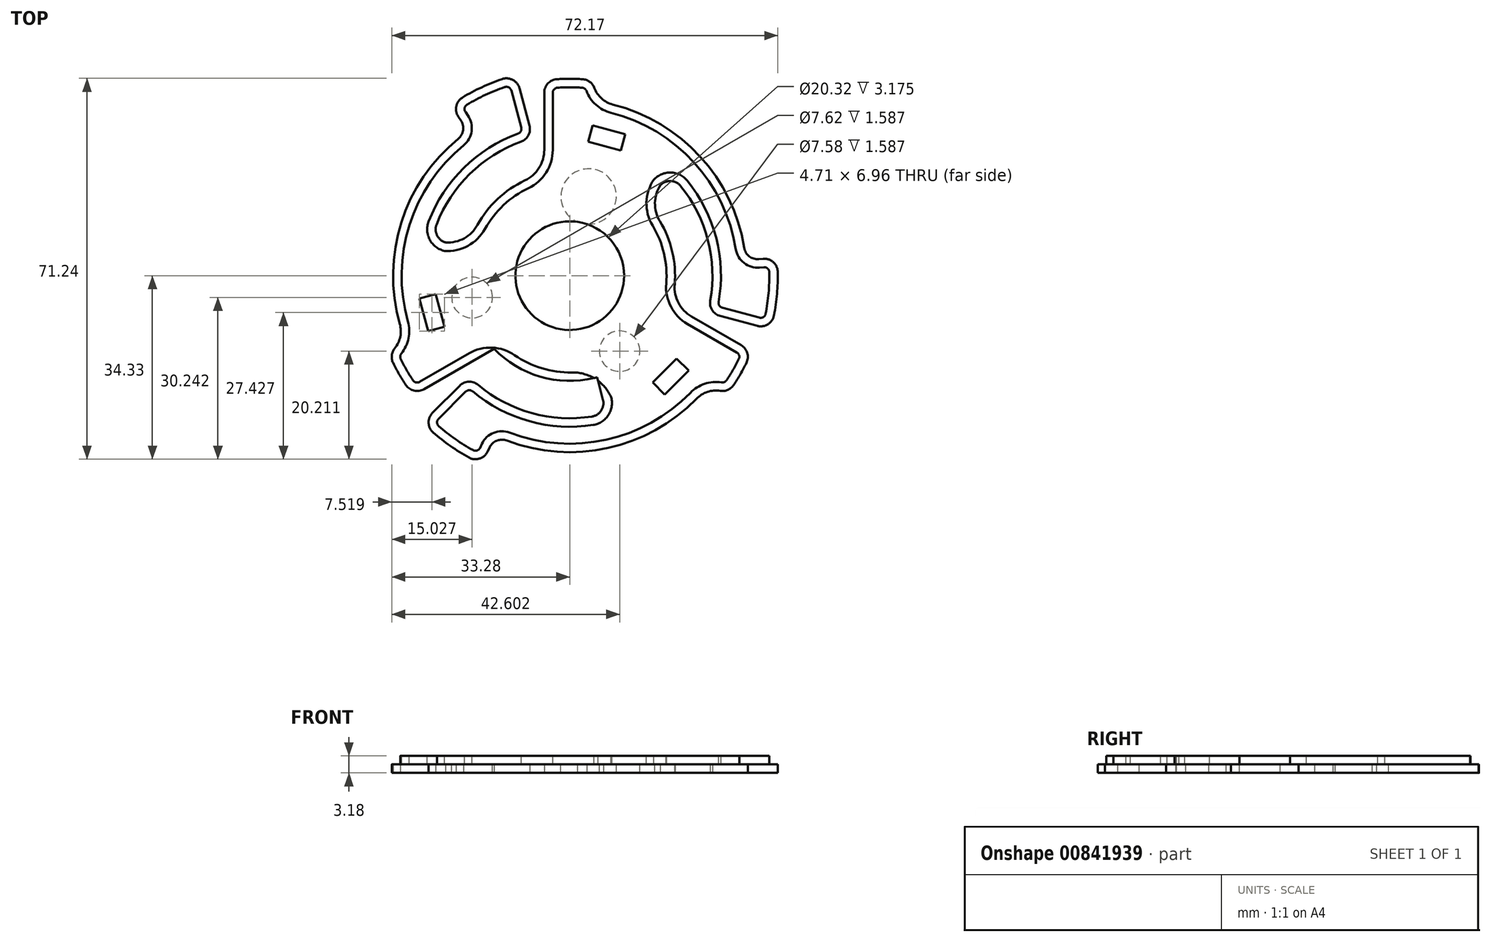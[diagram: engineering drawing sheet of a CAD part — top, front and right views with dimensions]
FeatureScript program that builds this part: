
annotation { "Feature Type Name" : "Feature", "Feature Type Description" : "" }
export const myFeature = defineFeature(function(context is Context, id is Id, definition is map)
    precondition{}
    {
        {
            var Q0;
            Q0=qCreatedBy(makeId("Top.planeOp"),FACE);
            var sketch = newSketch(context, id + "F0", { "sketchPlane" : qUnion([Q0])});
            skCircle(sketch, "E0", {"center": v(0, 0) * mm, "radius": 38.9 * mm, "construction": true});
            skCircle(sketch, "E1", {"center": v(0, 0) * mm, "radius": 36.83 * mm, "construction": true});
            skCircle(sketch, "E2", {"center": v(0, 0) * mm, "radius": 10.16 * mm});
            skCircle(sketch, "E3", {"center": v(0, 0) * mm, "radius": 19.69 * mm});
            skCircle(sketch, "E4", {"center": v(0, 0) * mm, "radius": 33.02 * mm, "construction": true});
            skLineSegment(sketch, "E5", {"start": v(-4.76, 19.1) * mm, "end": v(-4.76, 36.52) * mm});
            skLineSegment(sketch, "E6", {"start": v(0, 0) * mm, "end": v(0, 38.9) * mm, "construction": true});
            skLineSegment(sketch, "E7", {"start": v(4.76, 36.52) * mm, "end": v(4.76, 32.67) * mm});
            skArc(sketch, "E8", {"start": v(4.76, 36.52) * mm, "mid": v(0, 36.83) * mm, "end": v(-4.76, 36.52) * mm});
            skLineSegment(sketch, "E9", {"start": v(32.9, 2.88) * mm, "end": v(38.75, 3.39) * mm});
            skLineSegment(sketch, "E10", {"start": v(37.57, -10.07) * mm, "end": v(25.76, -6.9) * mm});
            skCircle(sketch, "E11.0", {"center": v(0, 0) * mm, "radius": 26.67 * mm, "construction": true});
            skArc(sketch, "E12", {"start": v(37.57, -10.07) * mm, "mid": v(38.75, -3.39) * mm, "end": v(38.75, 3.39) * mm});
            skArc(sketch, "E13", {"start": v(32.9, 2.88) * mm, "mid": v(24, 22.67) * mm, "end": v(4.76, 32.67) * mm});
            skArc(sketch, "E14", {"start": v(25.76, -6.9) * mm, "mid": v(25.76, 6.9) * mm, "end": v(18.86, 18.86) * mm});
            skLineSegment(sketch, "E15", {"start": v(18.86, 18.86) * mm, "end": v(13.92, 13.92) * mm});
            skLineSegment(sketch, "E16.bottom", {"start": v(9.56, 23.4) * mm, "end": v(3.43, 25.05) * mm});
            skLineSegment(sketch, "E16.top", {"start": v(10.38, 26.47) * mm, "end": v(4.25, 28.12) * mm});
            skLineSegment(sketch, "E16.left", {"start": v(9.56, 23.4) * mm, "end": v(10.38, 26.47) * mm});
            skLineSegment(sketch, "E16.right", {"start": v(3.43, 25.05) * mm, "end": v(4.25, 28.12) * mm});
            skPoint(sketch, "E16.middle", {"position": v(6.9, 25.76) * mm});
            skLineSegment(sketch, "E17", {"start": v(7.31, 27.3) * mm, "end": v(0, 0) * mm, "construction": true});
            skSolve(sketch);
        }
        {
            var Q0;
            {var subQ0=sQuery(id+"F0.wireOp",EDGE,"E5");Q0=makeQuery(id+"F0.imprint","IMPRINT",FACE,{"disambiguationData":[TD([[makeQuery(id+"F0.imprint","IMPRINT",EDGE,{"derivedFrom":subQ0}),-1.0]])]});}
            extrude(context, id + "F1", {"entities" : qUnion([Q0]), "depth" : 3.17 * mm, "offsetDistance" : 25.4 * mm});
        }
        {
            var Q0;
            Q0=makeQuery(id+"F1.opExtrude","SWEPT_EDGE",EDGE,{"disambiguationData":[OSD([sQuery(id+"F0.wireOp",EDGE,"E5"),sQuery(id+"F0.wireOp",EDGE,"E8")])]});
            var Q1;
            Q1=makeQuery(id+"F1.opExtrude","SWEPT_EDGE",EDGE,{"disambiguationData":[OSD([sQuery(id+"F0.wireOp",EDGE,"E7"),sQuery(id+"F0.wireOp",EDGE,"E8")])]});
            var Q2;
            Q2=makeQuery(id+"F1.opExtrude","SWEPT_EDGE",EDGE,{"disambiguationData":[OSD([sQuery(id+"F0.wireOp",EDGE,"E9"),sQuery(id+"F0.wireOp",EDGE,"E13")])]});
            var Q3;
            Q3=makeQuery(id+"F1.opExtrude","SWEPT_EDGE",EDGE,{"disambiguationData":[OSD([sQuery(id+"F0.wireOp",EDGE,"E9"),sQuery(id+"F0.wireOp",EDGE,"E12")])]});
            var Q4;
            Q4=makeQuery(id+"F1.opExtrude","SWEPT_EDGE",EDGE,{"disambiguationData":[OSD([sQuery(id+"F0.wireOp",EDGE,"E10"),sQuery(id+"F0.wireOp",EDGE,"E12")])]});
            var Q5;
            Q5=makeQuery(id+"F1.opExtrude","SWEPT_EDGE",EDGE,{"disambiguationData":[OSD([sQuery(id+"F0.wireOp",EDGE,"E10"),sQuery(id+"F0.wireOp",EDGE,"E14")])]});
            var Q6;
            Q6=makeQuery(id+"F1.opExtrude","SWEPT_EDGE",EDGE,{"disambiguationData":[OSD([sQuery(id+"F0.wireOp",EDGE,"E14"),sQuery(id+"F0.wireOp",EDGE,"E15")])]});
            fillet(context, id + "F2", {"entities" : qUnion([Q0, Q1, Q2, Q3, Q4, Q5, Q6]), "radius" : 2.54 * mm, "tangentPropagation" : true, "allowEdgeOverflow" : false});
        }
        {
            var Q0;
            Q0=makeQuery(id+"F1.opExtrude","SWEPT_EDGE",EDGE,{"disambiguationData":[OSD([sQuery(id+"F0.wireOp",EDGE,"E7"),sQuery(id+"F0.wireOp",EDGE,"E13")])]});
            fillet(context, id + "F3", {"entities" : qUnion([Q0]), "radius" : 5.08 * mm, "tangentPropagation" : true, "allowEdgeOverflow" : false});
        }
        {
            var Q0;
            Q0=makeQuery(id+"F1.opExtrude","SWEPT_BODY",BODY,{"disambiguationData":[OSD([sQuery(id+"F0.wireOp",EDGE,"E3"),sQuery(id+"F0.wireOp",EDGE,"E5"),sQuery(id+"F0.wireOp",EDGE,"E7"),sQuery(id+"F0.wireOp",EDGE,"E8"),sQuery(id+"F0.wireOp",EDGE,"E9"),sQuery(id+"F0.wireOp",EDGE,"E10"),sQuery(id+"F0.wireOp",EDGE,"E12"),sQuery(id+"F0.wireOp",EDGE,"E13"),sQuery(id+"F0.wireOp",EDGE,"E14"),sQuery(id+"F0.wireOp",EDGE,"E15")])]});
            var Q1;
            Q1=makeQuery(id+"F1.opExtrude","SWEPT_FACE",FACE,{"disambiguationData":[OSD([sQuery(id+"F0.wireOp",EDGE,"E3")])]});
            circularPattern(context, id + "F4", {"entities" : qUnion([Q0]), "axis" : qUnion([Q1]), "angle" : 360 * degree, "instanceCount" : 3, "oppositeDirection" : true, "equalSpace" : true});
        }
        {
            var Q0;
            Q0=makeQuery(id+"F0.imprint","IMPRINT",FACE,{"disambiguationData":[TD([[makeQuery(id+"F0.imprint","IMPRINT",EDGE,{"derivedFrom":sQuery(id+"F0.wireOp",EDGE,"E2")}),-1.0]])]});
            extrude(context, id + "F5", {"entities" : qUnion([Q0]), "operationType" : NewBodyOperationType.ADD, "depth" : 3.17 * mm, "offsetDistance" : 25.4 * mm});
        }
        {
            var Q0;
            Q0=makeQuery(id+"F1.opExtrude","SWEPT_EDGE",EDGE,{"disambiguationData":[OSD([sQuery(id+"F0.wireOp",EDGE,"E3"),sQuery(id+"F0.wireOp",EDGE,"E15")])]});
            var Q1;
            Q1=makeQuery(id+"F4.opPattern","COPY",EDGE,{"derivedFrom":makeQuery(id+"F1.opExtrude","SWEPT_EDGE",EDGE,{"disambiguationData":[OSD([sQuery(id+"F0.wireOp",EDGE,"E3"),sQuery(id+"F0.wireOp",EDGE,"E5")])]}),"instanceName":"1"});
            var Q2;
            Q2=makeQuery(id+"F4.opPattern","COPY",EDGE,{"derivedFrom":makeQuery(id+"F1.opExtrude","SWEPT_EDGE",EDGE,{"disambiguationData":[OSD([sQuery(id+"F0.wireOp",EDGE,"E3"),sQuery(id+"F0.wireOp",EDGE,"E15")])]}),"instanceName":"1"});
            var Q3;
            Q3=makeQuery(id+"F4.opPattern","COPY",EDGE,{"derivedFrom":makeQuery(id+"F1.opExtrude","SWEPT_EDGE",EDGE,{"disambiguationData":[OSD([sQuery(id+"F0.wireOp",EDGE,"E3"),sQuery(id+"F0.wireOp",EDGE,"E5")])]}),"instanceName":"2"});
            var Q4;
            Q4=makeQuery(id+"F4.opPattern","COPY",EDGE,{"derivedFrom":makeQuery(id+"F1.opExtrude","SWEPT_EDGE",EDGE,{"disambiguationData":[OSD([sQuery(id+"F0.wireOp",EDGE,"E3"),sQuery(id+"F0.wireOp",EDGE,"E15")])]}),"instanceName":"2"});
            var Q5;
            Q5=makeQuery(id+"F1.opExtrude","SWEPT_EDGE",EDGE,{"disambiguationData":[OSD([sQuery(id+"F0.wireOp",EDGE,"E3"),sQuery(id+"F0.wireOp",EDGE,"E5")])]});
            fillet(context, id + "F6", {"entities" : qUnion([Q0, Q1, Q2, Q3, Q4, Q5]), "radius" : 6.35 * mm, "tangentPropagation" : true, "allowEdgeOverflow" : false});
        }
        {
            var Q0;
            {var subQ0=sQuery(id+"F0.wireOp",EDGE,"E3");var subQ1=makeQuery(id+"F1.opExtrude","CAP_FACE",FACE,{"disambiguationData":[OSD([subQ0,sQuery(id+"F0.wireOp",EDGE,"E5"),sQuery(id+"F0.wireOp",EDGE,"E7"),sQuery(id+"F0.wireOp",EDGE,"E8"),sQuery(id+"F0.wireOp",EDGE,"E9"),sQuery(id+"F0.wireOp",EDGE,"E10"),sQuery(id+"F0.wireOp",EDGE,"E12"),sQuery(id+"F0.wireOp",EDGE,"E13"),sQuery(id+"F0.wireOp",EDGE,"E14"),sQuery(id+"F0.wireOp",EDGE,"E15")])],"isStart":false});Q0=makeQuery(id+"F5.boolean.opBoolean","MERGE",FACE,{"derivedFrom":[subQ1,makeQuery(id+"F4.opPattern","COPY",FACE,{"derivedFrom":subQ1,"instanceName":"1"}),makeQuery(id+"F4.opPattern","COPY",FACE,{"derivedFrom":subQ1,"instanceName":"2"}),makeQuery(id+"F5.opExtrude","CAP_FACE",FACE,{"disambiguationData":[OSD([sQuery(id+"F0.wireOp",EDGE,"E2"),subQ0])],"isStart":false})]});}
            var sketch = newSketch(context, id + "F7", { "sketchPlane" : qUnion([Q0])});
            skArc(sketch, "E18.0.0", {"start": v(20.74, 16.77) * mm, "mid": v(25.82, 6.67) * mm, "end": v(26.26, -4.64) * mm});
            skArc(sketch, "E18.0.1", {"start": v(26.26, -4.64) * mm, "mid": v(26.62, -6.44) * mm, "end": v(28.1, -7.53) * mm});
            skLineSegment(sketch, "E18.0.2", {"start": v(28.1, -7.53) * mm, "end": v(35.03, -9.39) * mm});
            skArc(sketch, "E18.0.3", {"start": v(35.03, -9.39) * mm, "mid": v(37.03, -9.09) * mm, "end": v(38.18, -7.42) * mm});
            skArc(sketch, "E18.0.4", {"start": v(38.18, -7.42) * mm, "mid": v(38.75, -3.39) * mm, "end": v(38.89, 0.67) * mm});
            skArc(sketch, "E18.0.5", {"start": v(38.89, 0.67) * mm, "mid": v(38.05, 2.52) * mm, "end": v(36.13, 3.16) * mm});
            skLineSegment(sketch, "E18.0.6", {"start": v(36.13, 3.16) * mm, "end": v(35.33, 3.1) * mm});
            skArc(sketch, "E18.0.7", {"start": v(35.33, 3.1) * mm, "mid": v(33.55, 3.62) * mm, "end": v(32.6, 5.22) * mm});
            skArc(sketch, "E18.0.8", {"start": v(32.6, 5.22) * mm, "mid": v(24.36, 22.29) * mm, "end": v(8.1, 32.01) * mm});
            skArc(sketch, "E18.0.9", {"start": v(8.1, 32.01) * mm, "mid": v(5.97, 33.14) * mm, "end": v(4.6, 35.12) * mm});
            skArc(sketch, "E18.0.10", {"start": v(4.6, 35.12) * mm, "mid": v(3.73, 36.26) * mm, "end": v(2.39, 36.75) * mm});
            skArc(sketch, "E18.0.11", {"start": v(2.39, 36.75) * mm, "mid": v(0, 36.83) * mm, "end": v(-2.39, 36.75) * mm});
            skArc(sketch, "E18.0.12", {"start": v(-2.39, 36.75) * mm, "mid": v(-4.08, 35.95) * mm, "end": v(-4.76, 34.22) * mm});
            skLineSegment(sketch, "E18.0.13", {"start": v(-4.76, 34.22) * mm, "end": v(-4.76, 23.54) * mm});
            skArc(sketch, "E18.0.14", {"start": v(-4.76, 23.54) * mm, "mid": v(-5.75, 20.14) * mm, "end": v(-8.4, 17.8) * mm});
            skArc(sketch, "E18.0.15", {"start": v(-8.4, 17.8) * mm, "mid": v(-13.48, 14.34) * mm, "end": v(-17.25, 9.49) * mm});
            skArc(sketch, "E18.0.16", {"start": v(-17.25, 9.49) * mm, "mid": v(-19.74, 7) * mm, "end": v(-23.18, 6.21) * mm});
            skArc(sketch, "E18.0.17", {"start": v(-23.18, 6.21) * mm, "mid": v(-24.78, 7.51) * mm, "end": v(-24.9, 9.58) * mm});
            skArc(sketch, "E18.0.18", {"start": v(-24.9, 9.58) * mm, "mid": v(-18.68, 19.03) * mm, "end": v(-9.12, 25.06) * mm});
            skArc(sketch, "E18.0.19", {"start": v(-9.12, 25.06) * mm, "mid": v(-7.73, 26.28) * mm, "end": v(-7.53, 28.1) * mm});
            skLineSegment(sketch, "E18.0.20", {"start": v(-7.53, 28.1) * mm, "end": v(-9.39, 35.03) * mm});
            skArc(sketch, "E18.0.21", {"start": v(-9.39, 35.03) * mm, "mid": v(-10.65, 36.61) * mm, "end": v(-12.67, 36.77) * mm});
            skArc(sketch, "E18.0.22", {"start": v(-12.67, 36.77) * mm, "mid": v(-16.44, 35.25) * mm, "end": v(-20.03, 33.34) * mm});
            skArc(sketch, "E18.0.23", {"start": v(-20.03, 33.34) * mm, "mid": v(-21.2, 31.7) * mm, "end": v(-20.8, 29.7) * mm});
            skLineSegment(sketch, "E18.0.24", {"start": v(-20.8, 29.7) * mm, "end": v(-20.34, 29.05) * mm});
            skArc(sketch, "E18.0.25", {"start": v(-20.34, 29.05) * mm, "mid": v(-19.9, 27.25) * mm, "end": v(-20.82, 25.63) * mm});
            skArc(sketch, "E18.0.26", {"start": v(-20.82, 25.63) * mm, "mid": v(-31.48, 9.96) * mm, "end": v(-31.77, -9) * mm});
            skArc(sketch, "E18.0.27", {"start": v(-31.77, -9) * mm, "mid": v(-31.68, -11.4) * mm, "end": v(-32.72, -13.58) * mm});
            skArc(sketch, "E18.0.28", {"start": v(-32.72, -13.58) * mm, "mid": v(-33.27, -14.9) * mm, "end": v(-33.02, -16.3) * mm});
            skArc(sketch, "E18.0.29", {"start": v(-33.02, -16.3) * mm, "mid": v(-31.9, -18.42) * mm, "end": v(-30.64, -20.44) * mm});
            skArc(sketch, "E18.0.30", {"start": v(-30.64, -20.44) * mm, "mid": v(-29.1, -21.5) * mm, "end": v(-27.25, -21.23) * mm});
            skLineSegment(sketch, "E18.0.31", {"start": v(-27.25, -21.23) * mm, "end": v(-18, -15.9) * mm});
            skArc(sketch, "E18.0.32", {"start": v(-18, -15.9) * mm, "mid": v(-14.57, -15.05) * mm, "end": v(-11.22, -16.18) * mm});
            skArc(sketch, "E18.0.33", {"start": v(-11.22, -16.18) * mm, "mid": v(-5.68, -18.85) * mm, "end": v(0.4, -19.68) * mm});
            skArc(sketch, "E18.0.34", {"start": v(0.4, -19.68) * mm, "mid": v(3.81, -20.6) * mm, "end": v(6.21, -23.18) * mm});
            skArc(sketch, "E18.0.35", {"start": v(6.21, -23.18) * mm, "mid": v(5.89, -25.22) * mm, "end": v(4.15, -26.34) * mm});
            skArc(sketch, "E18.0.36", {"start": v(4.15, -26.34) * mm, "mid": v(-7.14, -25.7) * mm, "end": v(-17.15, -20.43) * mm});
            skArc(sketch, "E18.0.37", {"start": v(-17.15, -20.43) * mm, "mid": v(-18.9, -19.83) * mm, "end": v(-20.58, -20.58) * mm});
            skLineSegment(sketch, "E18.0.38", {"start": v(-20.58, -20.58) * mm, "end": v(-25.64, -25.64) * mm});
            skArc(sketch, "E18.0.39", {"start": v(-25.64, -25.64) * mm, "mid": v(-26.39, -27.53) * mm, "end": v(-25.51, -29.36) * mm});
            skArc(sketch, "E18.0.40", {"start": v(-25.51, -29.36) * mm, "mid": v(-22.3, -31.86) * mm, "end": v(-18.86, -34.02) * mm});
            skArc(sketch, "E18.0.41", {"start": v(-18.86, -34.02) * mm, "mid": v(-16.84, -34.2) * mm, "end": v(-15.33, -32.87) * mm});
            skLineSegment(sketch, "E18.0.42", {"start": v(-15.33, -32.87) * mm, "end": v(-14.99, -32.15) * mm});
            skArc(sketch, "E18.0.43", {"start": v(-14.99, -32.15) * mm, "mid": v(-13.64, -30.87) * mm, "end": v(-11.78, -30.85) * mm});
            skArc(sketch, "E18.0.44", {"start": v(-11.78, -30.85) * mm, "mid": v(7.12, -32.24) * mm, "end": v(23.68, -23.02) * mm});
            skArc(sketch, "E18.0.45", {"start": v(23.68, -23.02) * mm, "mid": v(25.72, -21.74) * mm, "end": v(28.12, -21.54) * mm});
            skArc(sketch, "E18.0.46", {"start": v(28.12, -21.54) * mm, "mid": v(29.54, -21.36) * mm, "end": v(30.64, -20.44) * mm});
            skArc(sketch, "E18.0.47", {"start": v(30.64, -20.44) * mm, "mid": v(31.9, -18.41) * mm, "end": v(33.02, -16.3) * mm});
            skArc(sketch, "E18.0.48", {"start": v(33.02, -16.3) * mm, "mid": v(33.18, -14.45) * mm, "end": v(32.01, -12.98) * mm});
            skLineSegment(sketch, "E18.0.49", {"start": v(32.01, -12.98) * mm, "end": v(22.77, -7.65) * mm});
            skArc(sketch, "E18.0.50", {"start": v(22.77, -7.65) * mm, "mid": v(20.32, -5.1) * mm, "end": v(19.62, -1.62) * mm});
            skArc(sketch, "E18.0.51", {"start": v(19.62, -1.62) * mm, "mid": v(19.16, 4.5) * mm, "end": v(16.84, 10.2) * mm});
            skArc(sketch, "E18.0.52", {"start": v(16.84, 10.2) * mm, "mid": v(15.92, 13.6) * mm, "end": v(16.97, 16.97) * mm});
            skArc(sketch, "E18.0.53", {"start": v(16.97, 16.97) * mm, "mid": v(18.9, 17.7) * mm, "end": v(20.74, 16.77) * mm});
            skCircle(sketch, "E19.0", {"center": v(0, 0) * mm, "radius": 10.16 * mm});
            skArc(sketch, "E20.0", {"start": v(21.97, 17.77) * mm, "mid": v(27.36, 7.06) * mm, "end": v(27.83, -4.91) * mm});
            skArc(sketch, "E20.1", {"start": v(15.73, 17.97) * mm, "mid": v(18.9, 19.3) * mm, "end": v(21.97, 17.77) * mm});
            skArc(sketch, "E20.2", {"start": v(15.48, 9.37) * mm, "mid": v(14.34, 13.7) * mm, "end": v(15.73, 17.97) * mm});
            skArc(sketch, "E20.3", {"start": v(18.04, -1.5) * mm, "mid": v(17.62, 4.14) * mm, "end": v(15.48, 9.37) * mm});
            skArc(sketch, "E20.4", {"start": v(21.98, -9.02) * mm, "mid": v(18.91, -5.83) * mm, "end": v(18.04, -1.5) * mm});
            skLineSegment(sketch, "E20.5", {"start": v(31.22, -14.36) * mm, "end": v(21.98, -9.02) * mm});
            skArc(sketch, "E20.6", {"start": v(31.6, -15.6) * mm, "mid": v(31.66, -14.9) * mm, "end": v(31.22, -14.36) * mm});
            skArc(sketch, "E20.7", {"start": v(29.31, -19.56) * mm, "mid": v(30.52, -17.62) * mm, "end": v(31.6, -15.6) * mm});
            skArc(sketch, "E20.8", {"start": v(-12.15, 35.27) * mm, "mid": v(-15.77, 33.81) * mm, "end": v(-19.21, 31.98) * mm});
            skArc(sketch, "E20.9", {"start": v(-10.92, 34.62) * mm, "mid": v(-11.4, 35.21) * mm, "end": v(-12.15, 35.27) * mm});
            skLineSegment(sketch, "E20.10", {"start": v(-9.06, 27.7) * mm, "end": v(-10.92, 34.62) * mm});
            skArc(sketch, "E20.11", {"start": v(-9.66, 26.56) * mm, "mid": v(-9.14, 27.01) * mm, "end": v(-9.06, 27.7) * mm});
            skArc(sketch, "E20.12", {"start": v(-26.37, 10.15) * mm, "mid": v(-19.8, 20.16) * mm, "end": v(-9.66, 26.56) * mm});
            skArc(sketch, "E20.13", {"start": v(-23.42, 4.64) * mm, "mid": v(-26.16, 6.72) * mm, "end": v(-26.37, 10.15) * mm});
            skArc(sketch, "E20.14", {"start": v(-15.86, 8.72) * mm, "mid": v(-19.04, 5.57) * mm, "end": v(-23.42, 4.64) * mm});
            skArc(sketch, "E20.15", {"start": v(-7.72, 16.37) * mm, "mid": v(-12.4, 13.19) * mm, "end": v(-15.86, 8.72) * mm});
            skArc(sketch, "E20.16", {"start": v(-3.17, 23.54) * mm, "mid": v(-4.4, 19.3) * mm, "end": v(-7.72, 16.37) * mm});
            skLineSegment(sketch, "E20.17", {"start": v(-3.18, 34.22) * mm, "end": v(-3.18, 23.54) * mm});
            skArc(sketch, "E20.18", {"start": v(-2.28, 35.17) * mm, "mid": v(-2.92, 34.87) * mm, "end": v(-3.18, 34.22) * mm});
            skArc(sketch, "E20.19", {"start": v(2.28, 35.17) * mm, "mid": v(0, 35.24) * mm, "end": v(-2.28, 35.17) * mm});
            skArc(sketch, "E20.20", {"start": v(36.62, -7.11) * mm, "mid": v(37.16, -3.25) * mm, "end": v(37.3, 0.65) * mm});
            skArc(sketch, "E20.21", {"start": v(35.44, -7.85) * mm, "mid": v(36.2, -7.74) * mm, "end": v(36.62, -7.11) * mm});
            skLineSegment(sketch, "E20.22", {"start": v(28.52, -6) * mm, "end": v(35.44, -7.85) * mm});
            skArc(sketch, "E20.23", {"start": v(27.83, -4.91) * mm, "mid": v(27.96, -5.59) * mm, "end": v(28.52, -6) * mm});
            skArc(sketch, "E20.24", {"start": v(37.3, 0.65) * mm, "mid": v(36.99, 1.34) * mm, "end": v(36.27, 1.58) * mm});
            skLineSegment(sketch, "E20.25", {"start": v(36.27, 1.58) * mm, "end": v(35.47, 1.5) * mm});
            skArc(sketch, "E20.26", {"start": v(35.47, 1.5) * mm, "mid": v(32.57, 2.37) * mm, "end": v(31.04, 4.97) * mm});
            skArc(sketch, "E20.27", {"start": v(31.04, 4.97) * mm, "mid": v(23.2, 21.22) * mm, "end": v(7.7, 30.47) * mm});
            skArc(sketch, "E20.28", {"start": v(7.7, 30.47) * mm, "mid": v(4.91, 31.95) * mm, "end": v(3.11, 34.56) * mm});
            skArc(sketch, "E20.29", {"start": v(3.11, 34.56) * mm, "mid": v(2.79, 34.98) * mm, "end": v(2.28, 35.17) * mm});
            skArc(sketch, "E20.30", {"start": v(-19.21, 31.98) * mm, "mid": v(-19.65, 31.36) * mm, "end": v(-19.5, 30.62) * mm});
            skLineSegment(sketch, "E20.31", {"start": v(-19.5, 30.62) * mm, "end": v(-19.04, 29.97) * mm});
            skArc(sketch, "E20.32", {"start": v(-19.04, 29.97) * mm, "mid": v(-18.34, 27.03) * mm, "end": v(-19.82, 24.4) * mm});
            skArc(sketch, "E20.33", {"start": v(-19.82, 24.4) * mm, "mid": v(-29.97, 9.48) * mm, "end": v(-30.24, -8.56) * mm});
            skArc(sketch, "E20.34", {"start": v(-30.24, -8.56) * mm, "mid": v(-30.13, -11.72) * mm, "end": v(-31.48, -14.58) * mm});
            skArc(sketch, "E20.35", {"start": v(-31.48, -14.58) * mm, "mid": v(-31.7, -15.08) * mm, "end": v(-31.6, -15.6) * mm});
            skArc(sketch, "E20.36", {"start": v(-31.6, -15.6) * mm, "mid": v(-30.52, -17.62) * mm, "end": v(-29.31, -19.56) * mm});
            skArc(sketch, "E20.37", {"start": v(-29.31, -19.56) * mm, "mid": v(-28.74, -19.96) * mm, "end": v(-28.05, -19.86) * mm});
            skLineSegment(sketch, "E20.38", {"start": v(-28.05, -19.86) * mm, "end": v(-18.8, -14.52) * mm});
            skArc(sketch, "E20.39", {"start": v(-18.8, -14.52) * mm, "mid": v(-14.5, -13.47) * mm, "end": v(-10.31, -14.87) * mm});
            skArc(sketch, "E20.40", {"start": v(-10.31, -14.87) * mm, "mid": v(-5.22, -17.33) * mm, "end": v(0.37, -18.1) * mm});
            skArc(sketch, "E20.41", {"start": v(0.37, -18.1) * mm, "mid": v(4.7, -19.27) * mm, "end": v(7.7, -22.6) * mm});
            skArc(sketch, "E20.42", {"start": v(7.7, -22.6) * mm, "mid": v(7.26, -26.01) * mm, "end": v(4.4, -27.91) * mm});
            skArc(sketch, "E20.43", {"start": v(4.4, -27.91) * mm, "mid": v(-7.56, -27.23) * mm, "end": v(-18.17, -21.64) * mm});
            skArc(sketch, "E20.44", {"start": v(-18.17, -21.64) * mm, "mid": v(-18.82, -21.42) * mm, "end": v(-19.45, -21.7) * mm});
            skLineSegment(sketch, "E20.45", {"start": v(-19.45, -21.7) * mm, "end": v(-24.52, -26.77) * mm});
            skArc(sketch, "E20.46", {"start": v(-24.52, -26.77) * mm, "mid": v(-24.8, -27.47) * mm, "end": v(-24.47, -28.16) * mm});
            skArc(sketch, "E20.47", {"start": v(-24.47, -28.16) * mm, "mid": v(-21.4, -30.56) * mm, "end": v(-18.1, -32.63) * mm});
            skArc(sketch, "E20.48", {"start": v(-18.1, -32.63) * mm, "mid": v(-17.33, -32.7) * mm, "end": v(-16.76, -32.2) * mm});
            skLineSegment(sketch, "E20.49", {"start": v(-16.76, -32.2) * mm, "end": v(-16.43, -31.48) * mm});
            skArc(sketch, "E20.50", {"start": v(-16.43, -31.48) * mm, "mid": v(-14.24, -29.4) * mm, "end": v(-11.22, -29.36) * mm});
            skArc(sketch, "E20.51", {"start": v(-11.22, -29.36) * mm, "mid": v(6.78, -30.7) * mm, "end": v(22.54, -21.91) * mm});
            skArc(sketch, "E20.52", {"start": v(22.54, -21.91) * mm, "mid": v(25.22, -20.23) * mm, "end": v(28.37, -19.97) * mm});
            skArc(sketch, "E20.53", {"start": v(28.37, -19.97) * mm, "mid": v(28.9, -19.9) * mm, "end": v(29.31, -19.56) * mm});
            skCircle(sketch, "E21.0", {"center": v(0, 0) * mm, "radius": 11.75 * mm});
            skSolve(sketch);
        }
        {
            var Q0;
            Q0=makeQuery(id+"F7.imprint","IMPRINT",FACE,{"disambiguationData":[TD([[makeQuery(id+"F7.imprint","IMPRINT",EDGE,{"derivedFrom":sQuery(id+"F7.wireOp",EDGE,"E20.0")}),1.0]])]});
            extrude(context, id + "F8", {"entities" : qUnion([Q0]), "operationType" : NewBodyOperationType.REMOVE, "oppositeDirection" : true, "depth" : 1.59 * mm, "offsetDistance" : 25.4 * mm});
        }
        {
            var Q0;
            Q0=makeQuery(id+"F8.boolean.opBoolean","COPY",FACE,{"derivedFrom":makeQuery(id+"F8.opExtrude","CAP_FACE",FACE,{"disambiguationData":[OSD([sQuery(id+"F0.wireOp",EDGE,"E16.bottom"),sQuery(id+"F0.wireOp",EDGE,"E16.top"),sQuery(id+"F0.wireOp",EDGE,"E16.left"),sQuery(id+"F0.wireOp",EDGE,"E16.right"),sQuery(id+"F7.wireOp",EDGE,"E20.0"),sQuery(id+"F7.wireOp",EDGE,"E20.1"),sQuery(id+"F7.wireOp",EDGE,"E20.2"),sQuery(id+"F7.wireOp",EDGE,"E20.3"),sQuery(id+"F7.wireOp",EDGE,"E20.4"),sQuery(id+"F7.wireOp",EDGE,"E20.5"),sQuery(id+"F7.wireOp",EDGE,"E20.6"),sQuery(id+"F7.wireOp",EDGE,"E20.7"),sQuery(id+"F7.wireOp",EDGE,"E20.8"),sQuery(id+"F7.wireOp",EDGE,"E20.9"),sQuery(id+"F7.wireOp",EDGE,"E20.10"),sQuery(id+"F7.wireOp",EDGE,"E20.11"),sQuery(id+"F7.wireOp",EDGE,"E20.12"),sQuery(id+"F7.wireOp",EDGE,"E20.13"),sQuery(id+"F7.wireOp",EDGE,"E20.14"),sQuery(id+"F7.wireOp",EDGE,"E20.15"),sQuery(id+"F7.wireOp",EDGE,"E20.16"),sQuery(id+"F7.wireOp",EDGE,"E20.17"),sQuery(id+"F7.wireOp",EDGE,"E20.18"),sQuery(id+"F7.wireOp",EDGE,"E20.19"),sQuery(id+"F7.wireOp",EDGE,"E20.20"),sQuery(id+"F7.wireOp",EDGE,"E20.21"),sQuery(id+"F7.wireOp",EDGE,"E20.22"),sQuery(id+"F7.wireOp",EDGE,"E20.23"),sQuery(id+"F7.wireOp",EDGE,"E20.24"),sQuery(id+"F7.wireOp",EDGE,"E20.25"),sQuery(id+"F7.wireOp",EDGE,"E20.26"),sQuery(id+"F7.wireOp",EDGE,"E20.27"),sQuery(id+"F7.wireOp",EDGE,"E20.28"),sQuery(id+"F7.wireOp",EDGE,"E20.29"),sQuery(id+"F7.wireOp",EDGE,"E20.30"),sQuery(id+"F7.wireOp",EDGE,"E20.31"),sQuery(id+"F7.wireOp",EDGE,"E20.32"),sQuery(id+"F7.wireOp",EDGE,"E20.33"),sQuery(id+"F7.wireOp",EDGE,"E20.34"),sQuery(id+"F7.wireOp",EDGE,"E20.35"),sQuery(id+"F7.wireOp",EDGE,"E20.36"),sQuery(id+"F7.wireOp",EDGE,"E20.37"),sQuery(id+"F7.wireOp",EDGE,"E20.38"),sQuery(id+"F7.wireOp",EDGE,"E20.39"),sQuery(id+"F7.wireOp",EDGE,"E20.40"),sQuery(id+"F7.wireOp",EDGE,"E20.41"),sQuery(id+"F7.wireOp",EDGE,"E20.42"),sQuery(id+"F7.wireOp",EDGE,"E20.43"),sQuery(id+"F7.wireOp",EDGE,"E20.44"),sQuery(id+"F7.wireOp",EDGE,"E20.45"),sQuery(id+"F7.wireOp",EDGE,"E20.46"),sQuery(id+"F7.wireOp",EDGE,"E20.47"),sQuery(id+"F7.wireOp",EDGE,"E20.48"),sQuery(id+"F7.wireOp",EDGE,"E20.49"),sQuery(id+"F7.wireOp",EDGE,"E20.50"),sQuery(id+"F7.wireOp",EDGE,"E20.51"),sQuery(id+"F7.wireOp",EDGE,"E20.52"),sQuery(id+"F7.wireOp",EDGE,"E20.53"),sQuery(id+"F7.wireOp",EDGE,"E21.0")])],"isStart":false})});
            var sketch = newSketch(context, id + "F9", { "sketchPlane" : qUnion([Q0])});
            skCircle(sketch, "E22", {"center": v(9.32, -14.12) * mm, "radius": 3.79 * mm});
            skCircle(sketch, "E23", {"center": v(-18.25, -4.09) * mm, "radius": 3.81 * mm});
            skCircle(sketch, "E24", {"center": v(3.52, 14.81) * mm, "radius": 5.19 * mm});
            skSolve(sketch);
        }
        {
            var Q0;
            Q0=makeQuery(id+"F9.imprint","IMPRINT",FACE,{"disambiguationData":[TD([[makeQuery(id+"F9.imprint","IMPRINT",EDGE,{"derivedFrom":sQuery(id+"F9.wireOp",EDGE,"E22")}),1.0]])]});
            var Q1;
            Q1=makeQuery(id+"F9.imprint","IMPRINT",FACE,{"disambiguationData":[TD([[makeQuery(id+"F9.imprint","IMPRINT",EDGE,{"derivedFrom":sQuery(id+"F9.wireOp",EDGE,"E23")}),1.0]])]});
            var Q2;
            {var subQ0=sQuery(id+"F9.wireOp",EDGE,"E24");var subQ1=makeQuery(id+"F8.boolean.opBoolean","COPY",EDGE,{"derivedFrom":makeQuery(id+"F8.opExtrude","CAP_EDGE",EDGE,{"disambiguationData":[OSD([sQuery(id+"F7.wireOp",EDGE,"E21.0")])],"isStart":false})});var subQ2=makeQuery(id+"F9.imprint","INTERSECT",VERTEX,{"disambiguationData":[OD(0.0)],"derivedFrom":[subQ1,subQ0]});Q2=makeQuery(id+"F9.imprint","IMPRINT",FACE,{"disambiguationData":[TD([[makeQuery(id+"F9.imprint","IMPRINT",EDGE,{"disambiguationData":[TD([[subQ2,1.0]])],"derivedFrom":subQ0}),1.0]])]});}
            extrude(context, id + "F10", {"entities" : qUnion([Q0, Q1, Q2]), "operationType" : NewBodyOperationType.REMOVE, "oppositeDirection" : true, "depth" : 25.4 * mm, "offsetDistance" : 25.4 * mm});
        }
    });
